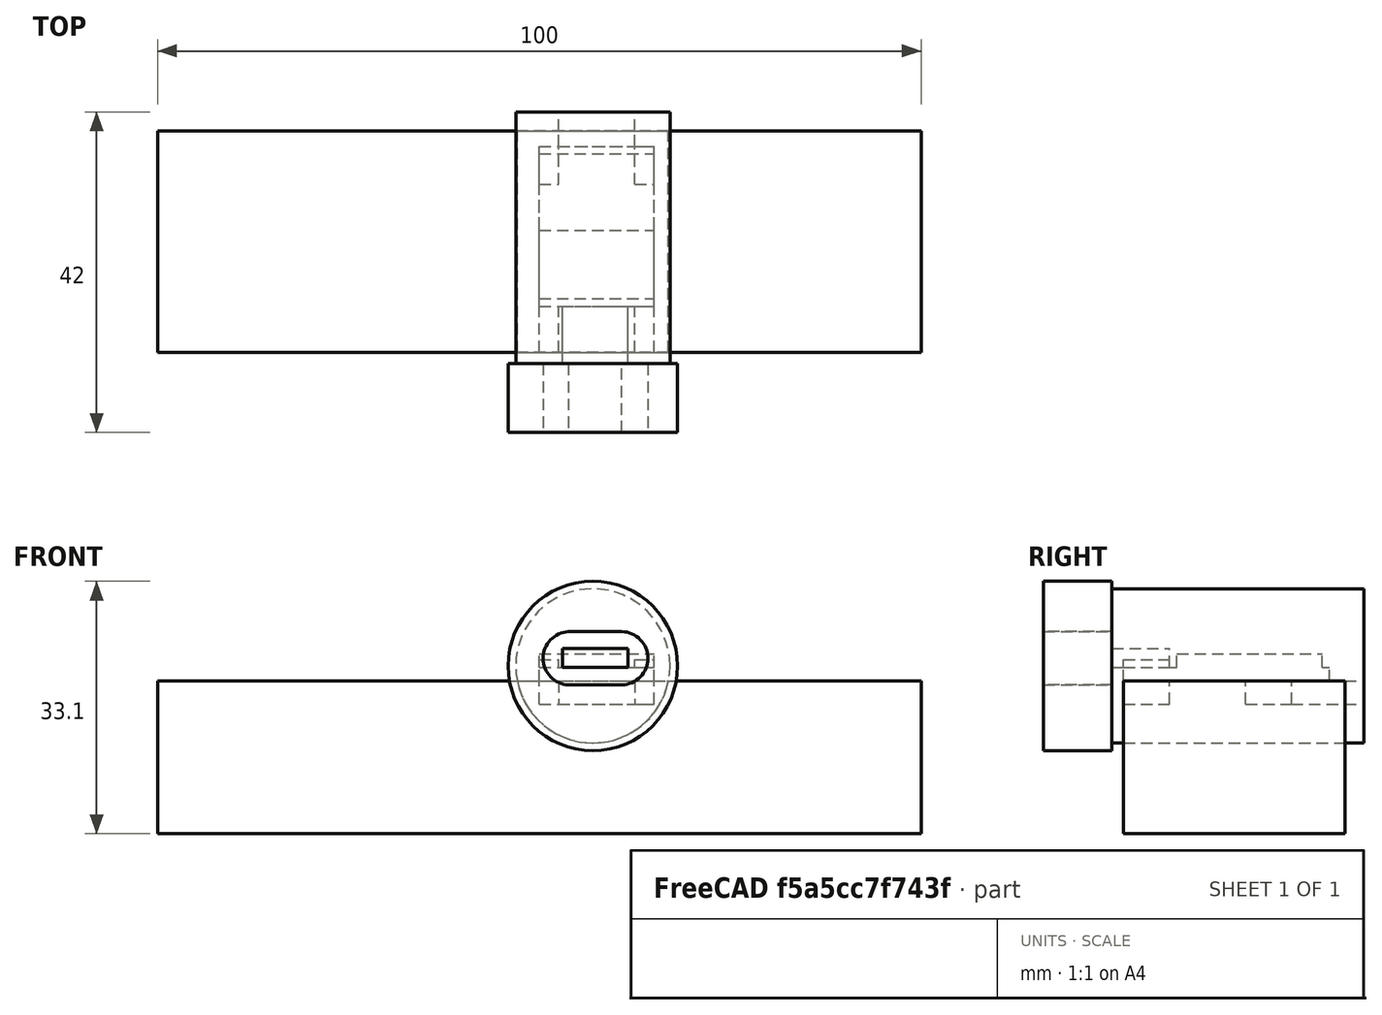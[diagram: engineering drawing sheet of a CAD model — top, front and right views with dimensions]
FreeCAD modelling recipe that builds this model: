
FCSTD DOCUMENT  (FreeCAD 0.17R13522 (Git))
Label: gaizi1
License: All rights reserved
LicenseURL: http://en.wikipedia.org/wiki/All_rights_reserved
objects: Part::Box×23, Part::Cylinder×8, Part::MultiFuse×7, Part::Cut×6
note: 44 computed .brp shape members not serialized (recipe doc carries the construction recipe); baked Part::Feature solids carry a one-line shape summary decoded from their .brp

FEATURE [Part::Box] Box  label="立方体"
  AttacherType = Attacher::AttachEngine3D
  Height = 1.8
  Length = 15
  Width = 27
FEATURE [Part::Box] Box001  label="立方体001"
  AttacherType = Attacher::AttachEngine3D
  Height = 1.8
  Length = 15
  Placement = pos=(0,7,1.8) rot=(0,0,1;0rad)
  Width = 19
FEATURE [Part::Box] Box002  label="立方体002"
  AttacherType = Attacher::AttachEngine3D
  Height = 2.5
  Length = 8.6
  Placement = pos=(3,-2,1.8) rot=(0,0,1;0rad)
  Width = 8
FEATURE [Part::Box] Box003  label="立方体003"
  AttacherType = Attacher::AttachEngine3D
  Height = 3
  Length = 15
  Placement = pos=(0,16,-3) rot=(0,0,1;0rad)
  Width = 6
FEATURE [Part::Box] Box004  label="立方体004"
  AttacherType = Attacher::AttachEngine3D
  Height = 3
  Length = 10
  Placement = pos=(2.5,22,-3) rot=(0,0,1;0rad)
  Width = 15
FEATURE [Part::Box] Box005  label="立方体005"
  AttacherType = Attacher::AttachEngine3D
  Height = 3
  Length = 15
  Placement = pos=(0,0,-3) rot=(0,0,1;0rad)
  Width = 6
FEATURE [Part::Cylinder] Cylinder  label="圆柱体"
  Angle = 360
  AttacherType = Attacher::AttachEngine3D
  Height = 33
  Placement = pos=(7,-0.5,2) rot=(-1,0,0;1.5708rad)
  Radius = 10.1
FEATURE [Part::Cylinder] Cylinder001  label="圆柱体001"
  Angle = 360
  AttacherType = Attacher::AttachEngine3D
  Height = 9
  Placement = pos=(7,-9.5,2) rot=(-1,0,0;1.5708rad)
  Radius = 11.1
FEATURE [Part::Box] Box006  label="立方体006"
  AttacherType = Attacher::AttachEngine3D
  Height = 1
  Length = 2.5
  Placement = pos=(0,0,1.8) rot=(0,0,1;0rad)
  Width = 6
FEATURE [Part::Box] Box007  label="立方体007"
  AttacherType = Attacher::AttachEngine3D
  Height = 1
  Length = 2.5
  Placement = pos=(12.5,0,1.8) rot=(0,0,1;0rad)
  Width = 6
FEATURE [Part::MultiFuse] Fusion
  Placement = pos=(0,1,0) rot=(0,0,1;0rad)
  Shapes = -> [Box006,Box002,Box001,Box004,Box003,Box,Box007,Box005]
FEATURE [Part::MultiFuse] Fusion001
  Shapes = -> [Cylinder001,Cylinder]
FEATURE [Part::Cut] Cut
  Base = -> Fusion001
  Tool = -> Fusion
FEATURE [Part::Box] Box008  label="立方体008"
  AttacherType = Attacher::AttachEngine3D
  Height = 20
  Length = 100
  Placement = pos=(-50,1,-20) rot=(0,0,1;0rad)
  Width = 29
FEATURE [Part::Box] Box009  label="立方体009"
  AttacherType = Attacher::AttachEngine3D
  Height = 7
  Length = 7
  Placement = pos=(3.8,-12,-0.5) rot=(0,0,1;0rad)
  Width = 12
FEATURE [Part::Cylinder] Cylinder002  label="圆柱体002"
  Angle = 360
  AttacherType = Attacher::AttachEngine3D
  Height = 12
  Placement = pos=(4,0,3) rot=(1,0,0;1.5708rad)
  Radius = 3.5
FEATURE [Part::Cylinder] Cylinder003  label="圆柱体003"
  Angle = 360
  AttacherType = Attacher::AttachEngine3D
  Height = 12
  Placement = pos=(10.7,0,3) rot=(1,0,0;1.5708rad)
  Radius = 3.5
FEATURE [Part::MultiFuse] Fusion002  label="插头屏蔽"
  Placement = pos=(0,-0.5,0) rot=(0,0,1;0rad)
  Shapes = -> [Box009,Cylinder002,Cylinder003]
FEATURE [Part::Cut] Cut001
  Base = -> Cut
  Tool = -> Fusion002
FEATURE [Part::Cut] Cut002  label="上"
  Base = -> Cut001
  Tool = -> Box008
FEATURE [Part::Box] Box010  label="立方体010"
  AttacherType = Attacher::AttachEngine3D
  Height = 40
  Length = 100
  Placement = pos=(-50,-99,-20) rot=(0,0,1;0rad)
  Width = 100
FEATURE [Part::Box] Box011  label="立方体011"
  AttacherType = Attacher::AttachEngine3D
  Height = 20
  Length = 100
  Placement = pos=(-50,1,0) rot=(0,0,1;0rad)
  Width = 29
FEATURE [Part::Box] Box012  label="立方体012"
  AttacherType = Attacher::AttachEngine3D
  Height = 40
  Length = 100
  Placement = pos=(-50,30,-20) rot=(0,0,1;0rad)
  Width = 100
FEATURE [Part::Cylinder] Cylinder004  label="圆柱体004"
  Angle = 360
  AttacherType = Attacher::AttachEngine3D
  Height = 12
  Placement = pos=(4,0,3) rot=(1,0,0;1.5708rad)
  Radius = 3.5
FEATURE [Part::Box] Box014  label="立方体014"
  AttacherType = Attacher::AttachEngine3D
  Height = 1.8
  Length = 15
  Width = 27
FEATURE [Part::Box] Box015  label="立方体015"
  AttacherType = Attacher::AttachEngine3D
  Height = 1.8
  Length = 15
  Placement = pos=(0,7,1.8) rot=(0,0,1;0rad)
  Width = 19
FEATURE [Part::Box] Box016  label="立方体016"
  AttacherType = Attacher::AttachEngine3D
  Height = 2.5
  Length = 8.6
  Placement = pos=(3,-2,1.8) rot=(0,0,1;0rad)
  Width = 8
FEATURE [Part::Box] Box017  label="立方体017"
  AttacherType = Attacher::AttachEngine3D
  Height = 3
  Length = 15
  Placement = pos=(0,16,-3) rot=(0,0,1;0rad)
  Width = 6
FEATURE [Part::Box] Box018  label="立方体018"
  AttacherType = Attacher::AttachEngine3D
  Height = 3
  Length = 10
  Placement = pos=(2.5,22,-3) rot=(0,0,1;0rad)
  Width = 15
FEATURE [Part::Box] Box019  label="立方体019"
  AttacherType = Attacher::AttachEngine3D
  Height = 3
  Length = 15
  Placement = pos=(0,0,-3) rot=(0,0,1;0rad)
  Width = 6
FEATURE [Part::Cylinder] Cylinder005  label="圆柱体005"
  Angle = 360
  AttacherType = Attacher::AttachEngine3D
  Height = 33
  Placement = pos=(7,-0.5,2) rot=(-1,0,0;1.5708rad)
  Radius = 10.1
FEATURE [Part::Box] Box020  label="立方体020"
  AttacherType = Attacher::AttachEngine3D
  Height = 1
  Length = 2.5
  Placement = pos=(0,0,1.8) rot=(0,0,1;0rad)
  Width = 6
FEATURE [Part::Cylinder] Cylinder006  label="圆柱体006"
  Angle = 360
  AttacherType = Attacher::AttachEngine3D
  Height = 10
  Placement = pos=(7,-10.5,2) rot=(-1,0,0;1.5708rad)
  Radius = 11.1
FEATURE [Part::MultiFuse] Fusion004
  Shapes = -> [Cylinder006,Cylinder005]
FEATURE [Part::Box] Box021  label="立方体021"
  AttacherType = Attacher::AttachEngine3D
  Height = 1
  Length = 2.5
  Placement = pos=(12.5,0,1.8) rot=(0,0,1;0rad)
  Width = 6
FEATURE [Part::MultiFuse] Fusion005
  Placement = pos=(0,1,0) rot=(0,0,1;0rad)
  Shapes = -> [Box020,Box016,Box015,Box018,Box017,Box014,Box021,Box019]
FEATURE [Part::Cut] Cut003
  Base = -> Fusion004
  Tool = -> Fusion005
FEATURE [Part::Box] Box022  label="立方体022"
  AttacherType = Attacher::AttachEngine3D
  Height = 20
  Length = 100
  Placement = pos=(-50,1,-20) rot=(0,0,1;0rad)
  Width = 29
FEATURE [Part::Cylinder] Cylinder007  label="圆柱体007"
  Angle = 360
  AttacherType = Attacher::AttachEngine3D
  Height = 12
  Placement = pos=(10.7,0,3) rot=(1,0,0;1.5708rad)
  Radius = 3.5
FEATURE [Part::Box] Box023  label="立方体023"
  AttacherType = Attacher::AttachEngine3D
  Height = 7
  Length = 20
  Placement = pos=(3.8,-12,-0.5) rot=(0,0,1;0rad)
  Width = 12
FEATURE [Part::MultiFuse] Fusion006  label="插头屏蔽001"
  Placement = pos=(0,-0.5,0) rot=(0,0,1;0rad)
  Shapes = -> [Box023,Cylinder004,Cylinder007]
FEATURE [Part::Cut] Cut004
  Base = -> Cut003
  Tool = -> Fusion006
FEATURE [Part::MultiFuse] Fusion007
  Shapes = -> [Box011,Box012,Box010]
FEATURE [Part::Cut] Cut005
  Base = -> Cut004
  Tool = -> Fusion007
